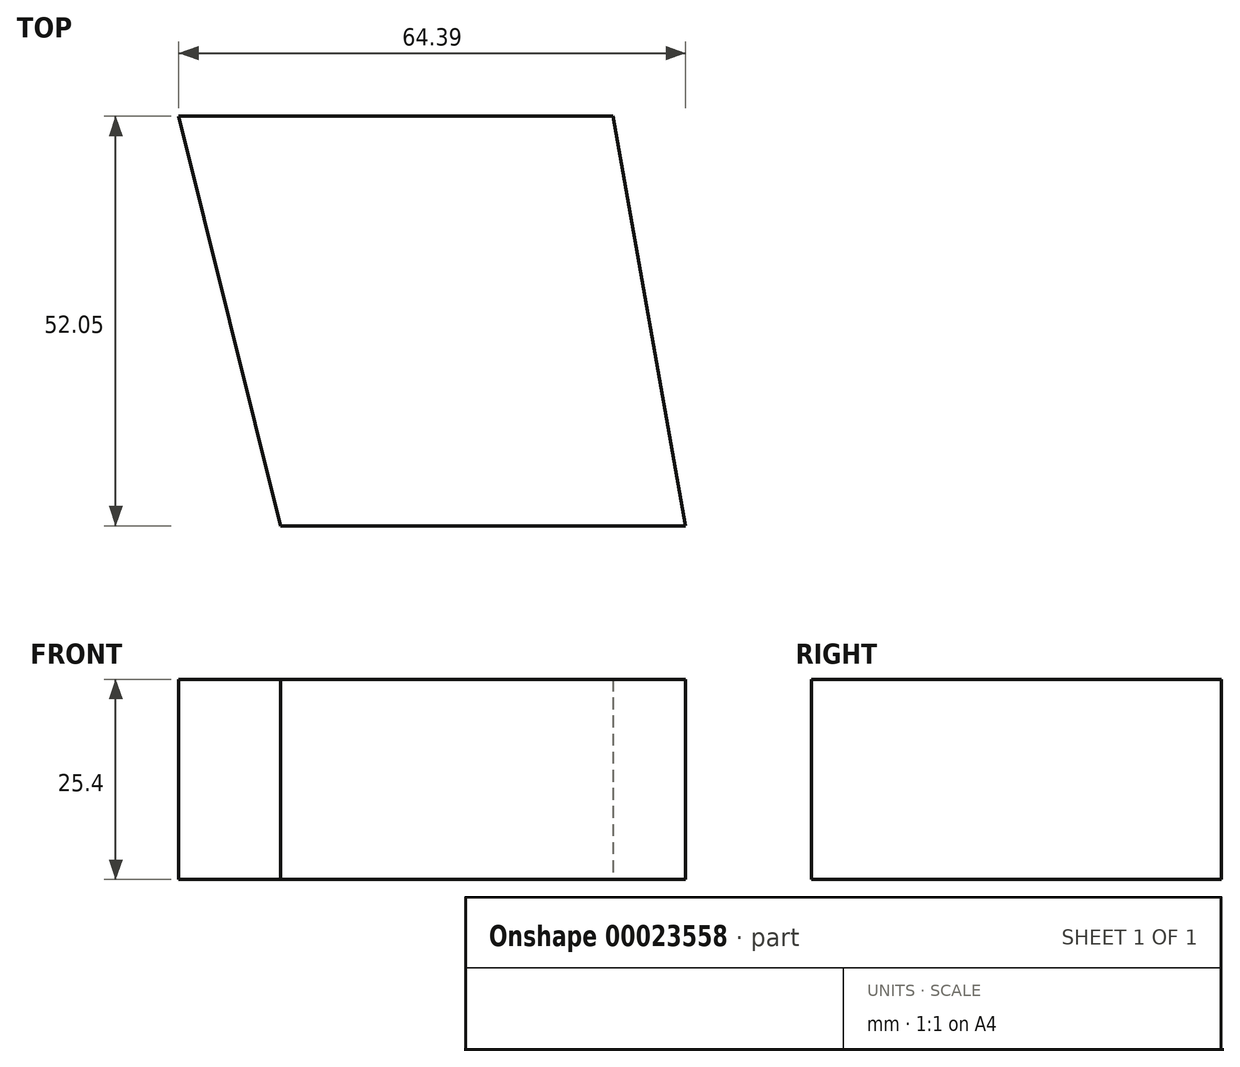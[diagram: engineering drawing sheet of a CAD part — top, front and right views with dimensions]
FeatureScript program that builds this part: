
annotation { "Feature Type Name" : "Feature", "Feature Type Description" : "" }
export const myFeature = defineFeature(function(context is Context, id is Id, definition is map)
    precondition{}
    {
        {
            var Q0;
            Q0=qCreatedBy(makeId("Top.planeOp"),FACE);
            var sketch = newSketch(context, id + "F0", { "sketchPlane" : qUnion([Q0])});
            skLineSegment(sketch, "E0", {"start": v(0, 0) * mm, "end": v(51.46, 0) * mm});
            skLineSegment(sketch, "E1", {"start": v(51.46, 0) * mm, "end": v(42.24, 52.05) * mm});
            skLineSegment(sketch, "E2", {"start": v(42.24, 52.05) * mm, "end": v(-12.93, 52.05) * mm});
            skLineSegment(sketch, "E3", {"start": v(-12.93, 52.05) * mm, "end": v(0, 0) * mm});
            skSolve(sketch);
        }
        {
            var Q0;
            Q0 = qSketchRegion(id + "F0", true);
            extrude(context, id + "F1", {"entities" : qUnion([Q0]), "depth" : 25.4 * mm});
        }
    });
